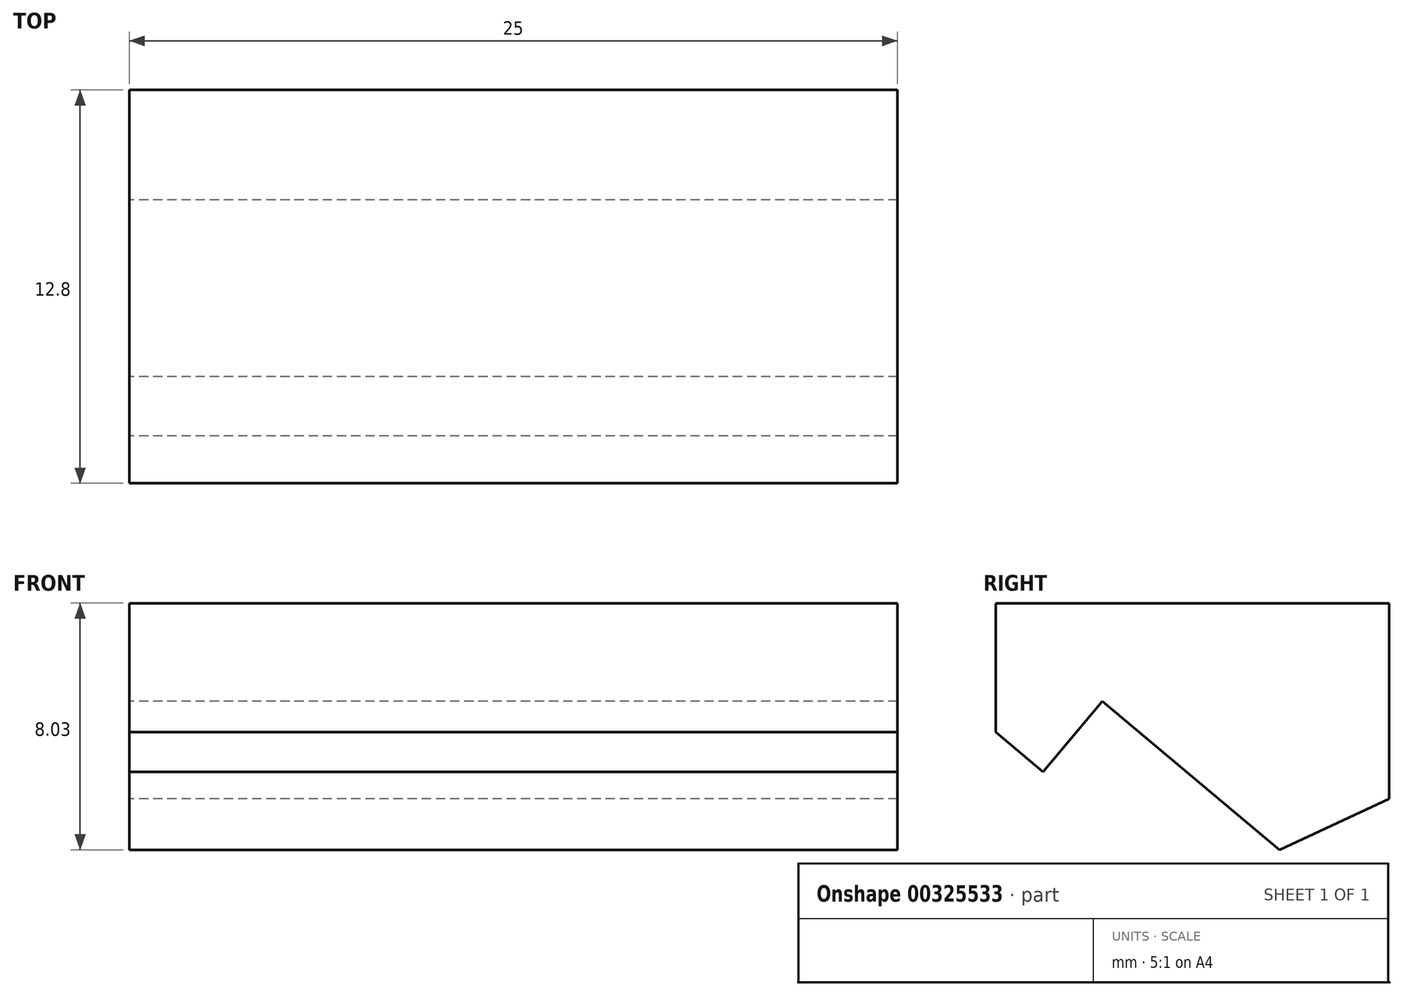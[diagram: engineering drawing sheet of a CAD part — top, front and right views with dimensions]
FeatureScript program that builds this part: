
annotation { "Feature Type Name" : "Feature", "Feature Type Description" : "" }
export const myFeature = defineFeature(function(context is Context, id is Id, definition is map)
    precondition{}
    {
        {
            var Q0;
            Q0=qCreatedBy(makeId("Right.planeOp"),FACE);
            var sketch = newSketch(context, id + "F0", { "sketchPlane" : qUnion([Q0])});
            skLineSegment(sketch, "E0", {"start": v(-4.35, 24.33) * mm, "end": v(8.45, 24.33) * mm});
            skLineSegment(sketch, "E1", {"start": v(8.45, 24.33) * mm, "end": v(8.45, 9.39) * mm});
            skLineSegment(sketch, "E2", {"start": v(8.45, 9.39) * mm, "end": v(-4.35, 20.13) * mm});
            skLineSegment(sketch, "E3", {"start": v(-4.35, 20.13) * mm, "end": v(-4.35, 24.33) * mm});
            skLineSegment(sketch, "E4", {"start": v(-2.81, 18.84) * mm, "end": v(-0.88, 21.13) * mm});
            skLineSegment(sketch, "E5", {"start": v(-0.88, 21.13) * mm, "end": v(5.78, 15.54) * mm});
            skLineSegment(sketch, "E6", {"start": v(5.78, 15.54) * mm, "end": v(3.85, 13.24) * mm});
            skSolve(sketch);
        }
        {
            var Q0;
            Q0=makeQuery(id+"F0.imprint","IMPRINT",FACE,{"disambiguationData":[TD([[makeQuery(id+"F0.imprint","IMPRINT",EDGE,{"derivedFrom":sQuery(id+"F0.wireOp",EDGE,"E0")}),-1.0]])]});
            extrude(context, id + "F1", {"entities" : qUnion([Q0]), "depth" : 25 * mm});
        }
        {
            var Q0;
            Q0=makeQuery(id+"F1.opExtrude","SWEPT_EDGE",EDGE,{"disambiguationData":[OSD([sQuery(id+"F0.wireOp",EDGE,"E1"),sQuery(id+"F0.wireOp",EDGE,"E2")])]});
            chamfer(context, id + "F2", {"entities" : qUnion([Q0]), "width" : 4 * mm, "tangentPropagation" : true});
        }
    });
